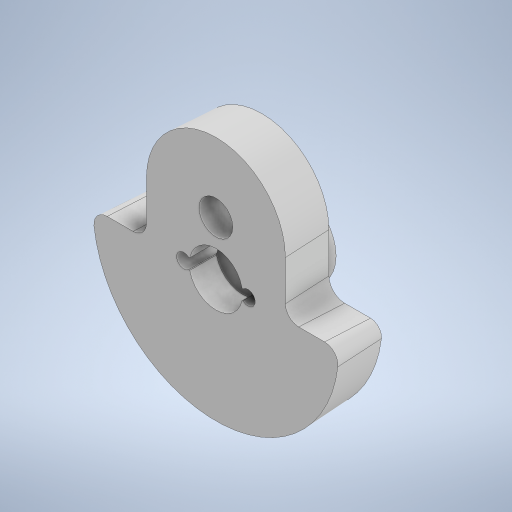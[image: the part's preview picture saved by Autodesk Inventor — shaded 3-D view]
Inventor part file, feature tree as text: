
AUTODESK INVENTOR PART (.ipt)
format: ipt  version: 2023 (Build 270158000, 158)  size: 543,232 bytes
history: native  units: in
note: dims shown in document units (in); Inventor stores cm internally (conversion verified against a paired STEP export)
features: extrude x8, fillet x2, draft x2, sketch x1
ambient origin geometry x8: Origin, YZ Plane, XZ Plane, XY Plane, X Axis, Y Axis, Z Axis, Center Point
bodies: Body1 (feature_tree)
feature tree (13):
  sketch  "Sketch1"  dims[d3=0.866in d15=0.75in d20=0.316in d37=0.75in d44=0.125in d57=0.74in d58=0.75in d59=0.0in d60=0.32in d61=0.0in d62=1.5in d63=0.0in d68=0.125in d70=0.135in d71=0.0206in d72=0.0412in d73=1.15in d76=0.3in d77=0.3in d78=1.0in d79=0.0in d80=1.0in d81=0.0in d84=0.5in d85=0.195in d86=0.5in d87=0.0in d88=0.5in d89=0.0in d90=0.5in d91=0.0in d92=0.005in]
  extrude  "Extrusion9"  Depth=0.005in
  extrude  "Extrusion10"  Depth=0.75in
  extrude  "Extrusion11"  Depth=0.125in
  fillet  "Fillet2"  Radius=0.74in
  draft  "FaceDraft1"
  draft  "FaceDraft2"
  extrude  "Extrusion14"  Depth=0.75in TaperAngle=0.0deg
  extrude  "Extrusion15"  Depth=0.32in TaperAngle=0.0deg
  extrude  "Extrusion17"  Depth=0.005in TaperAngle=0.0deg
  extrude  "Extrusion18"  Depth=0.125in
  extrude  "Extrusion19"  Depth=0.005in
  fillet  "Fillet3"  Radius=0.0206in
